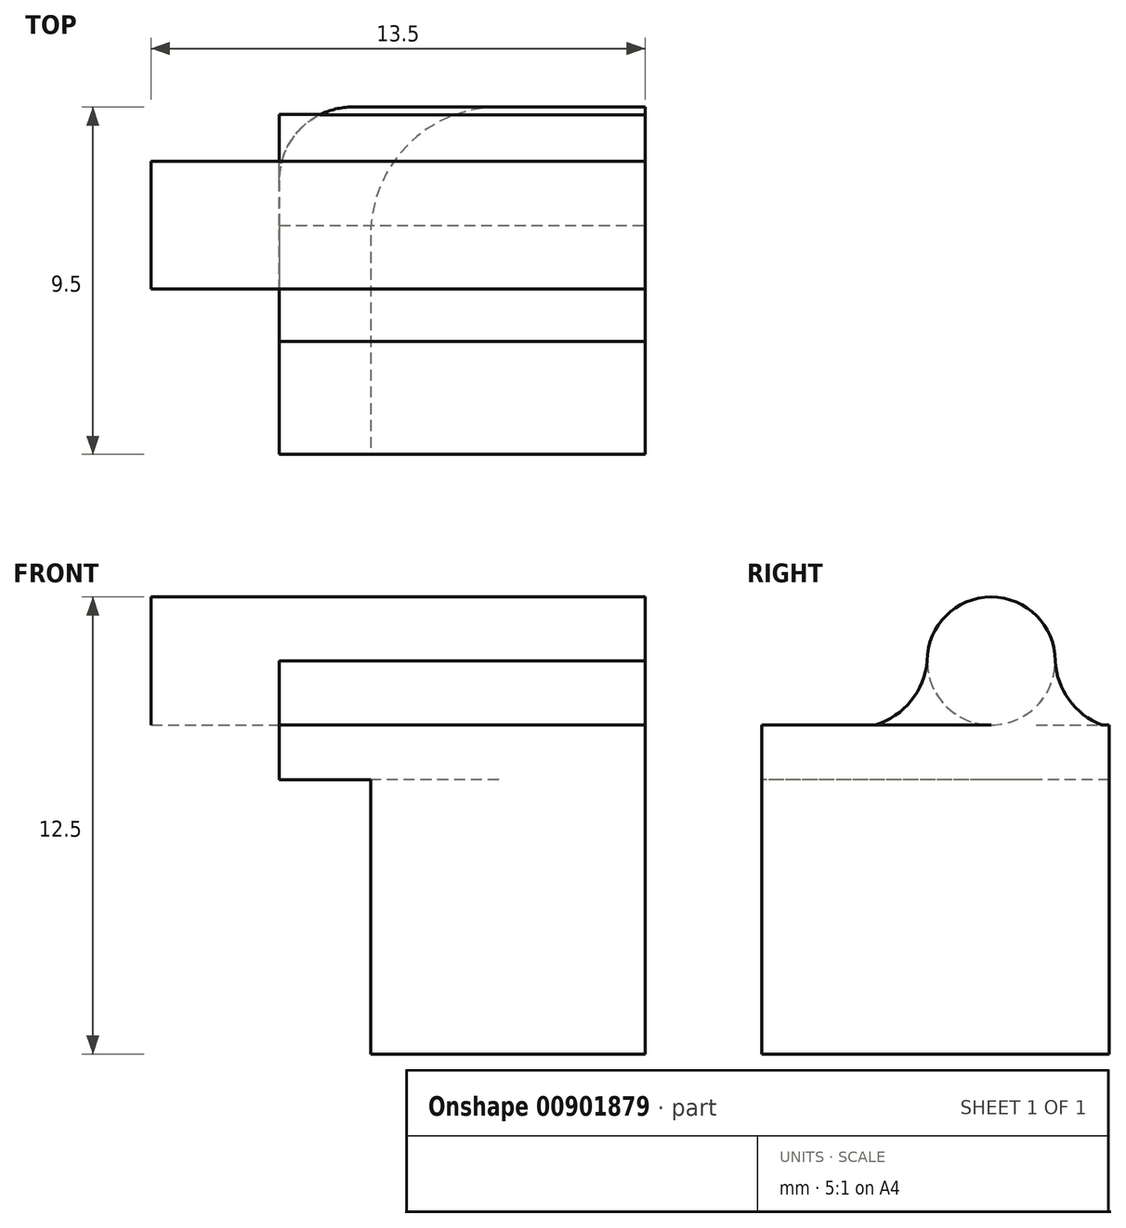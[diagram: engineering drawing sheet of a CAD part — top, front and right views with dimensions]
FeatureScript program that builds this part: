
annotation { "Feature Type Name" : "Feature", "Feature Type Description" : "" }
export const myFeature = defineFeature(function(context is Context, id is Id, definition is map)
    precondition{}
    {
        {
            var Q0;
            Q0=qCreatedBy(makeId("Top.planeOp"),FACE);
            var sketch = newSketch(context, id + "F0", { "sketchPlane" : qUnion([Q0])});
            skLineSegment(sketch, "E0.bottom", {"start": v(0, 5) * mm, "end": v(-4, 5) * mm});
            skLineSegment(sketch, "E0.top", {"start": v(0, -5) * mm, "end": v(-7.5, -5) * mm});
            skLineSegment(sketch, "E0.left", {"start": v(0, 5) * mm, "end": v(0, -5) * mm});
            skLineSegment(sketch, "E0.right", {"start": v(-7.5, 1.5) * mm, "end": v(-7.5, -5) * mm});
            skPoint(sketch, "E1.visualSharp", {"position": v(-7.5, 5) * mm});
            skArc(sketch, "E1.filletArc", {"start": v(-4, 5) * mm, "mid": v(-6.47, 3.97) * mm, "end": v(-7.5, 1.5) * mm});
            skLineSegment(sketch, "E2.bottom", {"start": v(0, 5) * mm, "end": v(-8, 5) * mm});
            skLineSegment(sketch, "E2.top", {"start": v(0, -4.5) * mm, "end": v(-10, -4.5) * mm});
            skLineSegment(sketch, "E2.left", {"start": v(0, 5) * mm, "end": v(0, -4.5) * mm});
            skLineSegment(sketch, "E2.right", {"start": v(-10, 3) * mm, "end": v(-10, -4.5) * mm});
            skPoint(sketch, "E3.visualSharp", {"position": v(-10, 5) * mm});
            skArc(sketch, "E3.filletArc", {"start": v(-8, 5) * mm, "mid": v(-9.41, 4.41) * mm, "end": v(-10, 3) * mm});
            skSolve(sketch);
        }
        {
            var Q0;
            Q0=makeQuery(id+"F0.imprint","IMPRINT",FACE,{"disambiguationData":[TD([[makeQuery(id+"F0.imprint","IMPRINT",EDGE,{"derivedFrom":sQuery(id+"F0.wireOp",EDGE,"E0.bottom")}),1.0]])]});
            extrude(context, id + "F1", {"entities" : qUnion([Q0]), "oppositeDirection" : true, "depth" : 7.5 * mm, "offsetDistance" : 25 * mm});
        }
        {
            var Q0;
            {var subQ5=sQuery(id+"F0.wireOp",EDGE,"E0.bottom");Q0=makeQuery(id+"F0.imprint","IMPRINT",FACE,{"disambiguationData":[TD([[makeQuery(id+"F0.imprint","IMPRINT",EDGE,{"derivedFrom":subQ5}),1.0]])]});}
            var Q1;
            {var subQ0=sQuery(id+"F0.wireOp",EDGE,"E1.filletArc");Q1=makeQuery(id+"F0.imprint","IMPRINT",FACE,{"disambiguationData":[TD([[makeQuery(id+"F0.imprint","IMPRINT",EDGE,{"derivedFrom":subQ0}),-1.0]])]});}
            extrude(context, id + "F2", {"entities" : qUnion([Q0, Q1]), "operationType" : NewBodyOperationType.ADD, "depth" : 1.5 * mm, "offsetDistance" : 25 * mm});
        }
        {
            var Q0;
            Q0=qCreatedBy(makeId("Right.planeOp"),FACE);
            var sketch = newSketch(context, id + "F3", { "sketchPlane" : qUnion([Q0])});
            skCircle(sketch, "E4", {"center": v(1.77, 3.25) * mm, "radius": 1.75 * mm});
            skLineSegment(sketch, "E5", {"start": v(-2.15, 1.5) * mm, "end": v(5.42, 1.5) * mm});
            skArc(sketch, "E6", {"start": v(3.52, 3.25) * mm, "mid": v(3.9, 2.18) * mm, "end": v(4.8, 1.5) * mm});
            skArc(sketch, "E7", {"start": v(-1.4, 1.5) * mm, "mid": v(-0.42, 2.16) * mm, "end": v(0.02, 3.25) * mm});
            skSolve(sketch);
        }
        {
            var Q0;
            {var subQ0=sQuery(id+"F3.wireOp",EDGE,"E4");var subQ1=makeQuery(id+"F3.imprint","INTERSECT",VERTEX,{"derivedFrom":[subQ0,sQuery(id+"F3.wireOp",EDGE,"E6")]});Q0=makeQuery(id+"F3.imprint","IMPRINT",FACE,{"disambiguationData":[TD([[makeQuery(id+"F3.imprint","IMPRINT",EDGE,{"disambiguationData":[TD([[subQ1,-1.0]])],"derivedFrom":subQ0}),1.0]])]});}
            var Q1;
            {var subQ0=sQuery(id+"F3.wireOp",EDGE,"E6");Q1=makeQuery(id+"F3.imprint","IMPRINT",FACE,{"disambiguationData":[TD([[makeQuery(id+"F3.imprint","IMPRINT",EDGE,{"derivedFrom":subQ0}),-1.0]])]});}
            var Q2;
            {var subQ0=sQuery(id+"F3.wireOp",EDGE,"E7");Q2=makeQuery(id+"F3.imprint","IMPRINT",FACE,{"disambiguationData":[TD([[makeQuery(id+"F3.imprint","IMPRINT",EDGE,{"derivedFrom":subQ0}),-1.0]])]});}
            extrude(context, id + "F4", {"entities" : qUnion([Q0, Q1, Q2]), "operationType" : NewBodyOperationType.ADD, "oppositeDirection" : true, "depth" : 10 * mm, "offsetDistance" : 25 * mm});
        }
        {
            var Q0;
            Q0=makeQuery(id+"F4.boolean.opBoolean","MERGE",FACE,{"derivedFrom":[makeQuery(id+"F2.opExtrude","SWEPT_FACE",FACE,{"disambiguationData":[OSD([sQuery(id+"F0.wireOp",EDGE,"E2.right")])]}),makeQuery(id+"F4.opExtrude","CAP_FACE",FACE,{"disambiguationData":[OSD([sQuery(id+"F3.wireOp",EDGE,"E4"),sQuery(id+"F3.wireOp",EDGE,"E5"),sQuery(id+"F3.wireOp",EDGE,"E6"),sQuery(id+"F3.wireOp",EDGE,"E7")])],"isStart":false})]});
            var sketch = newSketch(context, id + "F5", { "sketchPlane" : qUnion([Q0])});
            skCircle(sketch, "E8", {"center": v(-1.77, 3.25) * mm, "radius": 1.75 * mm});
            skSolve(sketch);
        }
        {
            var Q0;
            {var subQ0=sQuery(id+"F5.wireOp",EDGE,"E8");Q0=makeQuery(id+"F5.imprint","IMPRINT",FACE,{"disambiguationData":[TD([[makeQuery(id+"F5.imprint","IMPRINT",EDGE,{"disambiguationData":[OD(0.0)],"derivedFrom":subQ0}),-1.0]])]});}
            extrude(context, id + "F6", {"entities" : qUnion([Q0]), "operationType" : NewBodyOperationType.ADD, "depth" : 3.5 * mm, "offsetDistance" : 25 * mm});
        }
    });
